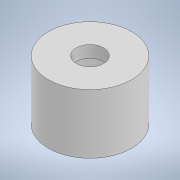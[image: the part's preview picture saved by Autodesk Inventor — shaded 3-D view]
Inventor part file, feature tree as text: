
AUTODESK INVENTOR PART (.ipt)
format: ipt  version: 2022 (Build 260153000, 153)  size: 108,032 bytes
history: native  units: mm
features: extrude x3, sketch x3
ambient origin geometry x8: Origin, YZ Plane, XZ Plane, XY Plane, X Axis, Y Axis, Z Axis, Center Point
bodies: Solid1 (feature_tree)
feature tree (6):
  extrude  "Extrusion1"  Depth=5.0mm TaperAngle=0.0deg
  extrude  "Extrusion3"  Depth=4.0mm TaperAngle=0.0deg
  extrude  "Extrusion4"  TaperAngle=0.0deg  [1 undecoded]
  sketch  "Sketch1"  dims[d0=7.0mm d1=5.0mm d2=0.0mm]
  sketch  "Sketch3"  dims[d6=0.8mm d7=4.0mm d8=0.0mm]
  sketch  "Sketch4"  dims[d9=2.3mm d10=0.0mm d11=0.0mm]
note: 1 required parameter value undecoded (feature->parameter linkage not recoverable at this tier; creation-order binding heuristic only, values carry confidence <= 0.55)
